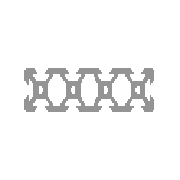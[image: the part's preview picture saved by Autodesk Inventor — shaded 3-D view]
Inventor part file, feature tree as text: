
AUTODESK INVENTOR PART (.ipt)
format: ipt  version: 2013 SP2 (Build 170200200, 200)  size: 264,192 bytes
history: native  units: mm
features: other x3, sketch x3, plane x1
ambient origin geometry x8: Origin, YZ Plane, XZ Plane, XY Plane, X Axis, Y Axis, Z Axis, Center Point
bodies: Solid1 (feature_tree), Body (feature_tree)
feature tree (7):
  other  "Driven Length"
  other  "Start Plane"
  other  "End Plane"
  sketch  "Sketch1"  dims[d0=10.0mm]
  sketch  "Sketch10"  dims[d1=10.0mm]
  plane  "Work Plane7"
  sketch  "Sketch11"  dims[d2=10.0mm d3=4.2mm d4=1.5mm d5=45.0deg d6=1.64mm d7=1.8mm d8=10.0mm d9=2.84mm d11=135.0deg d12=1.96mm d13=5.68mm d14=2.0mm d17=-0.0mm d18=10.0mm d19=0.13mm d20=0.0mm d29=90.0deg d22=10.0mm]
